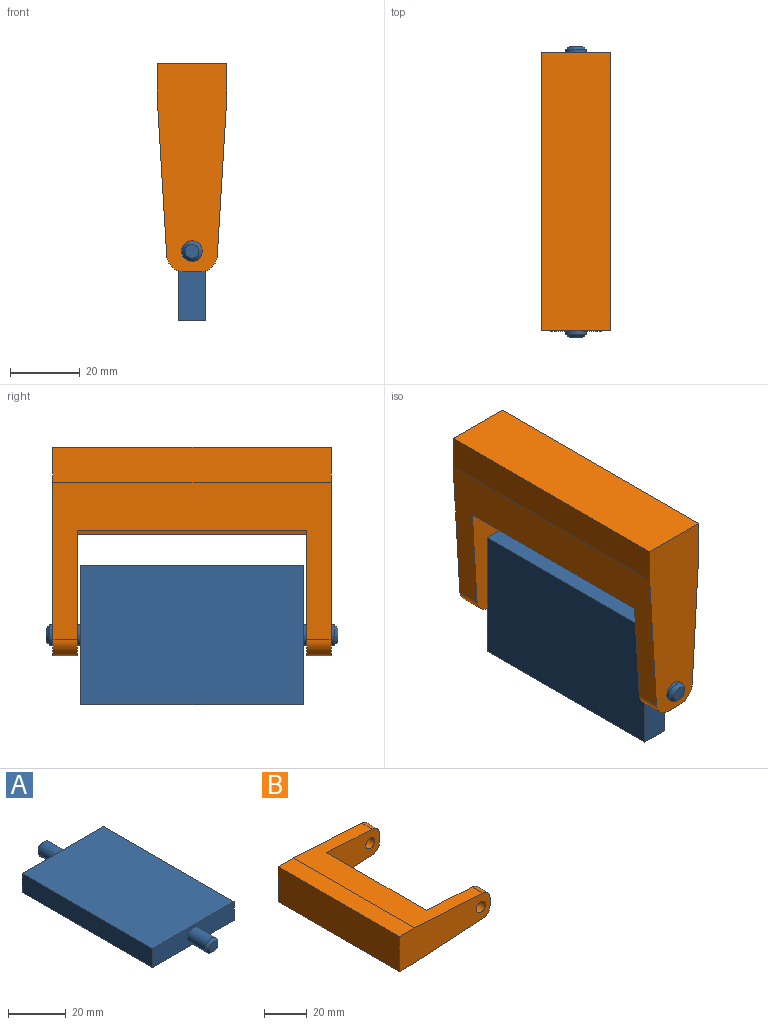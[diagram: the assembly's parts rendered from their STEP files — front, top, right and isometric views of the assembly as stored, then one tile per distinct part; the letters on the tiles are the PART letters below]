
ASSEMBLY  parts=2 mates=1
PART A: 12 faces, bbox 40x84x8 mm
  f0: plane 64x40mm, normal (0,0,1), area 2560mm2, adj f1,f3,f4,f5
  f1: plane 64x8mm, normal (-1,0,0), area 512mm2, adj f0,f2,f4,f5
  f2: plane 64x40mm, normal (0,0,-1), area 2560mm2, adj f1,f3,f4,f5
  f3: plane 64x8mm, normal (1,0,0), area 512mm2, adj f0,f2,f4,f5
  f4: plane 40x8mm, normal (0,-1,0), area 291.7mm2, adj f0,f1,f2,f3,f6
  f5: plane 40x8mm, normal (0,1,0), area 291.7mm2, adj f0,f1,f2,f3,f8
  f6: cylinder r=3mm len=9mm, axis (0,1,0), area 169.6mm2, adj f4,f10
  f7: plane 4x4mm, normal (0,-1,0), area 12.6mm2, adj f10
  f8: cylinder r=3mm len=9mm, axis (0,-1,0), area 169.6mm2, adj f5,f11
  f9: plane 4x4mm, normal (0,1,0), area 12.6mm2, adj f11
  f10: cone r=2mm half-angle=45deg, axis (0,1,0), area 22.2mm2, adj f6,f7
  f11: cone r=3mm half-angle=45deg, axis (0,-1,0), area 22.2mm2, adj f8,f9
PART B: 18 faces, bbox 60x80x20 mm
  f0: plane 80x45.3mm, normal (0.06,0,-1), area 1552.9mm2, adj f3,f6,f7,f8,f10,f11,f12,f16
  f1: plane 7x4.58mm, normal (1,0,0), area 32.1mm2, adj f3,f4,f7,f11
  f2: plane 80x45.3mm, normal (0.06,0,1), area 1625.3mm2, adj f4,f6,f7,f9,f10,f11,f12,f15
  f3: cylinder r=5mm len=7mm, axis (0,-1,0), area 52.9mm2, adj f0,f1,f7,f11
  f4: cylinder r=5mm len=7mm, axis (0,1,0), area 52.9mm2, adj f1,f2,f7,f11
  f5: plane 7x4.58mm, normal (1,0,0), area 32.1mm2, adj f6,f8,f9,f12
  f6: plane 60x20mm, normal (0,-1,0), area 1012.4mm2, adj f0,f2,f5,f8,f9,f13,f15,f16
  f7: plane 60x20mm, normal (0,1,0), area 1012.4mm2, adj f0,f1,f2,f3,f4,f14,f15,f16
  f8: cylinder r=5mm len=7mm, axis (0,-1,0), area 52.9mm2, adj f0,f5,f6,f12
  f9: cylinder r=5mm len=7mm, axis (0,1,0), area 52.9mm2, adj f2,f5,f6,f12
  f10: plane 66x18.27mm, normal (1,0,-0.06), area 1207.9mm2, adj f0,f2,f11,f12
  f11: plane 36.12x18.27mm, normal (0,-1,0), area 536.4mm2, adj f0,f1,f2,f3,f4,f10,f14
  f12: plane 36.12x18.27mm, normal (0,1,0), area 536.4mm2, adj f0,f2,f5,f8,f9,f10,f13
  f13: cylinder r=3mm len=7mm, axis (0,-1,0), area 131.9mm2, adj f6,f12
  f14: cylinder r=3mm len=7mm, axis (0,-1,0), area 131.9mm2, adj f7,f11
  f15: plane 80x10mm, normal (0,0,1), area 800mm2, adj f2,f6,f7,f17
  f16: plane 80x10mm, normal (0,0,-1), area 800mm2, adj f0,f6,f7,f17
  f17: plane 80x20mm, normal (-1,0,0), area 1600mm2, adj f6,f7,f15,f16
PLACE A rot(axis=(0,1,0),90deg) t=(22.82,0.83,-0.31)mm
PLACE B rot(axis=(0,1,0),90deg) t=(32.82,0.83,23.69)mm
MATE revolute A.f6 <-> B.f13  axis (0,-1,0) through (22.82,-31.17,-20.31)mm
